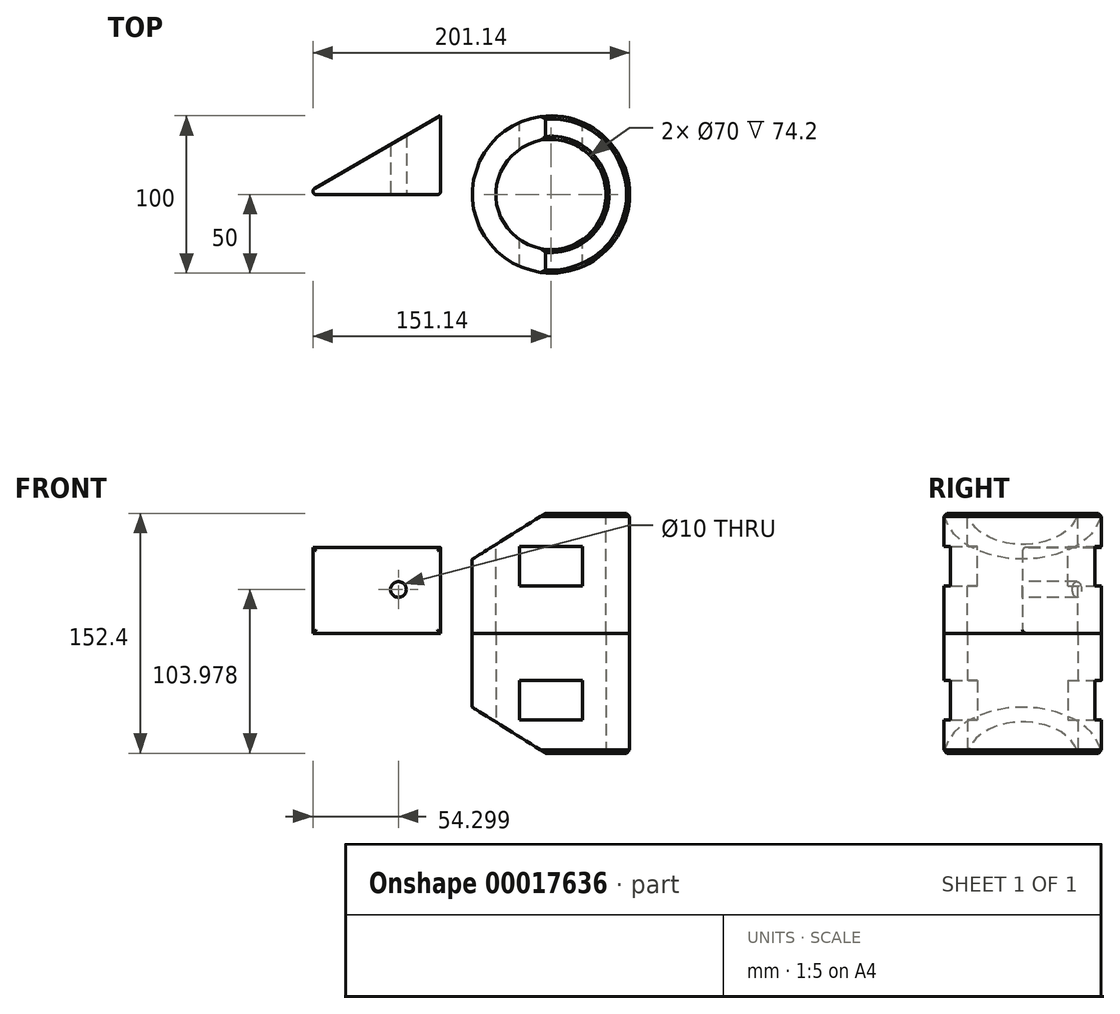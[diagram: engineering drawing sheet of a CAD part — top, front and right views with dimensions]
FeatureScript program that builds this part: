
annotation { "Feature Type Name" : "Feature", "Feature Type Description" : "" }
export const myFeature = defineFeature(function(context is Context, id is Id, definition is map)
    precondition{}
    {
        {
            var Q0;
            Q0=qCreatedBy(makeId("Top.planeOp"),FACE);
            var sketch = newSketch(context, id + "F0", { "sketchPlane" : qUnion([Q0])});
            skCircle(sketch, "E0", {"center": v(0, 0) * mm, "radius": 50 * mm});
            skSolve(sketch);
        }
        {
            var Q0;
            Q0=makeQuery(id+"F0.imprint","IMPRINT",FACE,{"disambiguationData":[TD([[makeQuery(id+"F0.imprint","IMPRINT",EDGE,{"derivedFrom":sQuery(id+"F0.wireOp",EDGE,"E0")}),1.0]])]});
            extrude(context, id + "F1", {"entities" : qUnion([Q0]), "depth" : 76.2 * mm});
        }
        {
            var Q0;
            Q0=makeQuery(id+"F1.opExtrude","CAP_FACE",FACE,{"disambiguationData":[OSD([sQuery(id+"F0.wireOp",EDGE,"E0")])],"isStart":false});
            var sketch = newSketch(context, id + "F2", { "sketchPlane" : qUnion([Q0])});
            skCircle(sketch, "E1", {"center": v(0, 0) * mm, "radius": 35 * mm});
            skSolve(sketch);
        }
        {
            var Q0;
            Q0=makeQuery(id+"F2.imprint","IMPRINT",FACE,{"disambiguationData":[TD([[makeQuery(id+"F2.imprint","IMPRINT",EDGE,{"derivedFrom":sQuery(id+"F2.wireOp",EDGE,"E1")}),1.0]])]});
            extrude(context, id + "F3", {"entities" : qUnion([Q0]), "operationType" : NewBodyOperationType.REMOVE, "endBound" : BoundingType.THROUGH_ALL, "oppositeDirection" : true, "depth" : 25.4 * mm});
        }
        {
            var Q0;
            Q0=qCreatedBy(makeId("Front.planeOp"),FACE);
            var sketch = newSketch(context, id + "F4", { "sketchPlane" : qUnion([Q0])});
            skLineSegment(sketch, "E2.bottom", {"start": v(-20, 30) * mm, "end": v(20, 30) * mm});
            skLineSegment(sketch, "E2.top", {"start": v(-20, 55) * mm, "end": v(20, 55) * mm});
            skLineSegment(sketch, "E2.left", {"start": v(-20, 30) * mm, "end": v(-20, 55) * mm});
            skLineSegment(sketch, "E2.right", {"start": v(20, 30) * mm, "end": v(20, 55) * mm});
            skSolve(sketch);
        }
        {
            var Q0;
            Q0=makeQuery(id+"F4.imprint","IMPRINT",FACE,{"disambiguationData":[TD([[makeQuery(id+"F4.imprint","IMPRINT",EDGE,{"derivedFrom":sQuery(id+"F4.wireOp",EDGE,"E2.bottom")}),1.0]])]});
            extrude(context, id + "F5", {"entities" : qUnion([Q0]), "operationType" : NewBodyOperationType.REMOVE, "depth" : 273.83 * mm, "symmetric" : true});
        }
        {
            var Q0;
            Q0=makeQuery(id+"F1.opExtrude","CAP_FACE",FACE,{"disambiguationData":[OSD([sQuery(id+"F0.wireOp",EDGE,"E0")])],"isStart":false});
            chamfer(context, id + "F6", {"entities" : qUnion([Q0]), "width" : 2 * mm, "tangentPropagation" : true});
        }
        {
            var Q0;
            Q0=qCreatedBy(makeId("Front.planeOp"),FACE);
            var sketch = newSketch(context, id + "F7", { "sketchPlane" : qUnion([Q0])});
            skLineSegment(sketch, "E3", {"start": v(0, 78.33) * mm, "end": v(-70, 34.36) * mm});
            skLineSegment(sketch, "E4", {"start": v(-70, 34.36) * mm, "end": v(-70, 78.33) * mm});
            skLineSegment(sketch, "E5", {"start": v(-70, 78.33) * mm, "end": v(0, 78.33) * mm});
            skSolve(sketch);
        }
        {
            var Q0;
            Q0=makeQuery(id+"F7.imprint","IMPRINT",FACE,{"disambiguationData":[TD([[makeQuery(id+"F7.imprint","IMPRINT",EDGE,{"derivedFrom":sQuery(id+"F7.wireOp",EDGE,"E3")}),-1.0]])]});
            extrude(context, id + "F8", {"entities" : qUnion([Q0]), "operationType" : NewBodyOperationType.REMOVE, "oppositeDirection" : true, "depth" : 145.75 * mm, "symmetric" : true});
        }
        {
            var Q0;
            Q0=makeQuery(id+"F1.opExtrude","SWEPT_BODY",BODY,{"disambiguationData":[OSD([sQuery(id+"F0.wireOp",EDGE,"E0")])]});
            var Q1;
            Q1=qCreatedBy(makeId("Top.planeOp"),FACE);
            mirror(context, id + "F9", {"entities" : qUnion([Q0]), "mirrorPlane" : qUnion([Q1])});
        }
        {
            var Q0;
            Q0=qCreatedBy(makeId("Top.planeOp"),FACE);
            var sketch = newSketch(context, id + "F10", { "sketchPlane" : qUnion([Q0])});
            skLineSegment(sketch, "E6", {"start": v(-70, 50) * mm, "end": v(-70, 0) * mm});
            skLineSegment(sketch, "E7", {"start": v(-70, 0) * mm, "end": v(-156.6, 0) * mm});
            skLineSegment(sketch, "E8", {"start": v(-156.6, 0) * mm, "end": v(-70, 50) * mm});
            skSolve(sketch);
        }
        {
            var Q0;
            Q0=makeQuery(id+"F10.imprint","IMPRINT",FACE,{"disambiguationData":[TD([[makeQuery(id+"F10.imprint","IMPRINT",EDGE,{"derivedFrom":sQuery(id+"F10.wireOp",EDGE,"E6")}),-1.0]])]});
            extrude(context, id + "F11", {"entities" : qUnion([Q0]), "depth" : 54.42 * mm});
        }
        {
            var Q0;
            Q0=makeQuery(id+"F11.opExtrude","SWEPT_FACE",FACE,{"disambiguationData":[OSD([sQuery(id+"F10.wireOp",EDGE,"E7")])]});
            fillet(context, id + "F12", {"entities" : qUnion([Q0]), "radius" : 2 * mm, "tangentPropagation" : true, "allowEdgeOverflow" : false});
        }
        {
            var Q0;
            Q0=makeQuery(id+"F11.opExtrude","SWEPT_FACE",FACE,{"disambiguationData":[OSD([sQuery(id+"F10.wireOp",EDGE,"E7")])]});
            var sketch = newSketch(context, id + "F13", { "sketchPlane" : qUnion([Q0])});
            skCircle(sketch, "E9", {"center": v(-96.84, 27.78) * mm, "radius": 5 * mm});
            skSolve(sketch);
        }
        {
            var Q0;
            Q0=makeQuery(id+"F13.imprint","IMPRINT",FACE,{"disambiguationData":[TD([[makeQuery(id+"F13.imprint","IMPRINT",EDGE,{"derivedFrom":sQuery(id+"F13.wireOp",EDGE,"E9")}),1.0]])]});
            extrude(context, id + "F14", {"entities" : qUnion([Q0]), "operationType" : NewBodyOperationType.REMOVE, "endBound" : BoundingType.UP_TO_NEXT, "oppositeDirection" : true, "depth" : 25 * mm});
        }
    });
